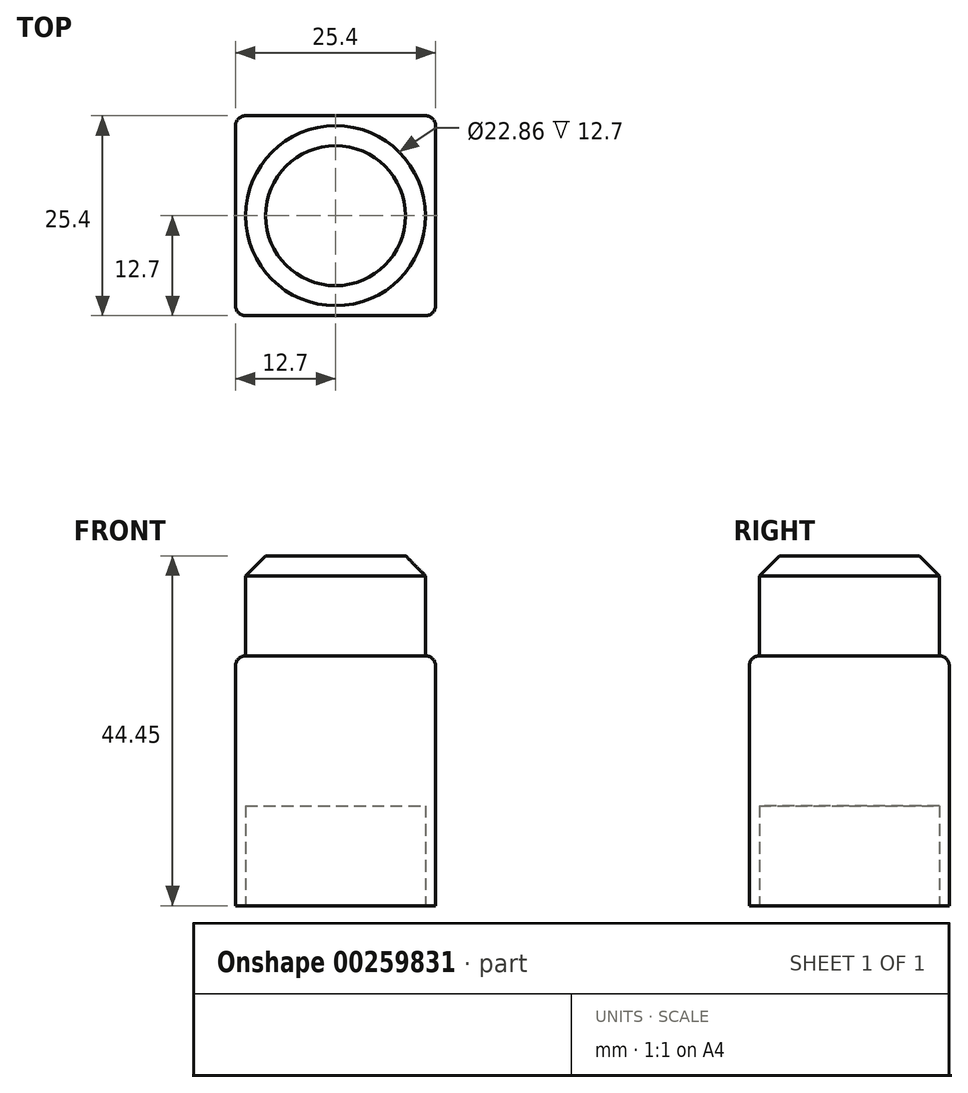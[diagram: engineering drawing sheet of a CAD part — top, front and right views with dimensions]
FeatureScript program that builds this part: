
annotation { "Feature Type Name" : "Feature", "Feature Type Description" : "" }
export const myFeature = defineFeature(function(context is Context, id is Id, definition is map)
    precondition{}
    {
        {
            var Q0;
            Q0=qCreatedBy(makeId("Top.planeOp"),FACE);
            var sketch = newSketch(context, id + "F0", { "sketchPlane" : qUnion([Q0])});
            skLineSegment(sketch, "E0.bottom", {"start": v(12.7, 12.7) * mm, "end": v(-12.7, 12.7) * mm});
            skLineSegment(sketch, "E0.top", {"start": v(12.7, -12.7) * mm, "end": v(-12.7, -12.7) * mm});
            skLineSegment(sketch, "E0.left", {"start": v(12.7, 12.7) * mm, "end": v(12.7, -12.7) * mm});
            skLineSegment(sketch, "E0.right", {"start": v(-12.7, 12.7) * mm, "end": v(-12.7, -12.7) * mm});
            skPoint(sketch, "E0.middle", {"position": v(0, 0) * mm});
            skSolve(sketch);
        }
        {
            var Q0;
            Q0 = qSketchRegion(id + "F0", true);
            extrude(context, id + "F1", {"entities" : qUnion([Q0]), "depth" : 31.75 * mm});
        }
        {
            var Q0;
            Q0=makeQuery(id+"F1.opExtrude","CAP_FACE",FACE,{"disambiguationData":[OSD([sQuery(id+"F0.wireOp",EDGE,"E0.bottom"),sQuery(id+"F0.wireOp",EDGE,"E0.top"),sQuery(id+"F0.wireOp",EDGE,"E0.left"),sQuery(id+"F0.wireOp",EDGE,"E0.right")])],"isStart":false});
            var sketch = newSketch(context, id + "F2", { "sketchPlane" : qUnion([Q0])});
            skCircle(sketch, "E1", {"center": v(0, 0) * mm, "radius": 11.43 * mm});
            skSolve(sketch);
        }
        {
            var Q0;
            Q0 = qSketchRegion(id + "F2", true);
            extrude(context, id + "F3", {"entities" : qUnion([Q0]), "operationType" : NewBodyOperationType.ADD, "depth" : 12.7 * mm});
        }
        {
            var Q0;
            Q0=makeQuery(id+"F3.opExtrude","CAP_EDGE",EDGE,{"disambiguationData":[OSD([sQuery(id+"F2.wireOp",EDGE,"E1")])],"isStart":false});
            chamfer(context, id + "F4", {"entities" : qUnion([Q0]), "width" : 2.54 * mm, "tangentPropagation" : true});
        }
        {
            var Q0;
            Q0=makeQuery(id+"F1.opExtrude","SWEPT_EDGE",EDGE,{"disambiguationData":[OSD([sQuery(id+"F0.wireOp",EDGE,"E0.top"),sQuery(id+"F0.wireOp",EDGE,"E0.right")])]});
            var Q1;
            Q1=makeQuery(id+"F1.opExtrude","SWEPT_EDGE",EDGE,{"disambiguationData":[OSD([sQuery(id+"F0.wireOp",EDGE,"E0.top"),sQuery(id+"F0.wireOp",EDGE,"E0.left")])]});
            var Q2;
            Q2=makeQuery(id+"F1.opExtrude","SWEPT_EDGE",EDGE,{"disambiguationData":[OSD([sQuery(id+"F0.wireOp",EDGE,"E0.bottom"),sQuery(id+"F0.wireOp",EDGE,"E0.right")])]});
            var Q3;
            Q3=makeQuery(id+"F1.opExtrude","SWEPT_EDGE",EDGE,{"disambiguationData":[OSD([sQuery(id+"F0.wireOp",EDGE,"E0.bottom"),sQuery(id+"F0.wireOp",EDGE,"E0.left")])]});
            fillet(context, id + "F5", {"entities" : qUnion([Q0, Q1, Q2, Q3]), "radius" : 1.27 * mm, "tangentPropagation" : true, "allowEdgeOverflow" : false});
        }
        {
            var Q0;
            Q0=makeQuery(id+"F1.opExtrude","CAP_EDGE",EDGE,{"disambiguationData":[OSD([sQuery(id+"F0.wireOp",EDGE,"E0.top")])],"isStart":false});
            var Q1;
            Q1=makeQuery(id+"F1.opExtrude","CAP_EDGE",EDGE,{"disambiguationData":[OSD([sQuery(id+"F0.wireOp",EDGE,"E0.left")])],"isStart":false});
            var Q2;
            Q2=makeQuery(id+"F1.opExtrude","CAP_EDGE",EDGE,{"disambiguationData":[OSD([sQuery(id+"F0.wireOp",EDGE,"E0.bottom")])],"isStart":false});
            var Q3;
            Q3=makeQuery(id+"F1.opExtrude","CAP_EDGE",EDGE,{"disambiguationData":[OSD([sQuery(id+"F0.wireOp",EDGE,"E0.right")])],"isStart":false});
            fillet(context, id + "F6", {"entities" : qUnion([Q0, Q1, Q2, Q3]), "radius" : 1.27 * mm, "tangentPropagation" : true, "allowEdgeOverflow" : false});
        }
        {
            var Q0;
            Q0=makeQuery(id+"F1.opExtrude","CAP_FACE",FACE,{"disambiguationData":[OSD([sQuery(id+"F0.wireOp",EDGE,"E0.bottom"),sQuery(id+"F0.wireOp",EDGE,"E0.top"),sQuery(id+"F0.wireOp",EDGE,"E0.left"),sQuery(id+"F0.wireOp",EDGE,"E0.right")])],"isStart":true});
            var sketch = newSketch(context, id + "F7", { "sketchPlane" : qUnion([Q0])});
            skCircle(sketch, "E2", {"center": v(0, 0) * mm, "radius": 11.43 * mm});
            skSolve(sketch);
        }
        {
            var Q0;
            Q0 = qSketchRegion(id + "F7", true);
            extrude(context, id + "F8", {"entities" : qUnion([Q0]), "operationType" : NewBodyOperationType.REMOVE, "oppositeDirection" : true, "depth" : 12.7 * mm});
        }
    });
